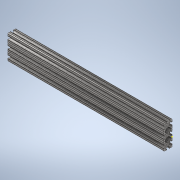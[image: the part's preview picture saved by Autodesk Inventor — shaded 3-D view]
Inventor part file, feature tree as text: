
AUTODESK INVENTOR PART (.ipt)
format: ipt  version: 2020 (Build 240168000, 168)  size: 381,952 bytes
history: native  units: in
note: dims shown in document units (in); Inventor stores cm internally (conversion verified against a paired STEP export)
features: sketch x2, extrude x1
ambient origin geometry x8: Origin, YZ Plane, XZ Plane, XY Plane, X Axis, Y Axis, Z Axis, Center Point
bodies: Solid1 (feature_tree)
feature tree (3):
  extrude  "Extrusion1"  [1 undecoded]
  sketch  "Sketch2"
  sketch  "Sketch1"  dims[d0=19.0in d1=0.0in]
note: 1 required parameter value undecoded (feature->parameter linkage not recoverable at this tier; creation-order binding heuristic only, values carry confidence <= 0.55)
